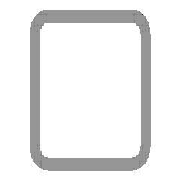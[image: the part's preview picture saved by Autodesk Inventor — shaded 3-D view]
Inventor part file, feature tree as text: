
AUTODESK INVENTOR PART (.ipt)
format: ipt  version: 2022 (Build 260153000, 153)  size: 632,320 bytes
history: native  units: mm (DEFAULTED — no unit token found)
features: other x8, sketch x3, plane x2, surface_op x2, split x1
ambient origin geometry x8: Origin, YZ Plane, XZ Plane, XY Plane, X Axis, Y Axis, Z Axis, Center Point
bodies: Solid1 (feature_tree), Body (feature_tree), Solid7 (feature_tree), Solid8 (feature_tree)
feature tree (16):
  parser-record x1  (decoder bookkeeping rows leaked as tree rows — omitted from the tree; the rows remain in map.json)
  other  "Driven Length"
  other  "Start Plane"
  other  "End Plane"
  plane  "Work Plane4"
  split  "Split1"
  sketch  "Sketch"  dims[d7=4.0mm d9=40.0mm d11=40.0mm d12=2.0mm d13=20.0mm d14=330.0mm d15=20.0mm d16=20.0mm d17=90.0deg d18=310.0mm d73=5.0mm d74=5.0mm d75=5.0mm d76=5.0mm d77=5.0mm d78=5.0mm d79=5.0mm d80=5.0mm d81=0.0mm d82=5.0mm d83=5.0mm d84=5.0mm d85=5.0mm d86=5.0mm d87=5.0mm d88=5.0mm d89=5.0mm d90=0.0mm]
  sketch  "Sketch3"  dims[d3=310.0mm]
  plane  "Work Plane3"
  sketch  "Sketch4"  dims[d4=0.0mm]
  other  "Srf13"
  other  "Srf14"
  other  "Srf12"
  surface_op  "Boundary Patch7"
  surface_op  "Boundary Patch8"
  other  "Srf15"
